# Revit family: HOSPITAIR SCROLAIR 2
name_source: partatom
category: Equipement de génie climatique
revit_build: Autodesk Revit 2018 (Build: 20170223_1515(x64)
units: mm (PartAtom-declared; Revit-internal decimal feet)

## family parameters
Basée sur le plan de construction = Non
Classification = Aucun
Cote de connecteur circulaire = Utiliser le diamètre
Couper avec des vides une fois chargée = Non
Partagée = Non
Point de calcul de pièce = Non
Toujours verticalement = Oui
Type d'élément = Normal

## types (12) — shared parameters
BRANCHEMENT_TERRE = Oui
COS_PHI = 0.9
DIAM_REFOUL_AIR = 20 mm  [stored 0.0656168 ft]
DOUBLE_ALIMENTATION = Oui
LARGEUR = 1135 mm  [stored 3.72375 ft]
NBR_POLES = 1
NEUTRE = Oui
TENSION_ALIM = 400 V
Zone de Maintenance = 600 mm  [stored 1.9685 ft]
Zone de maintenance = Oui
Zone de maintenance_Hauteur = 1565 mm  [stored 5.13451 ft]

## per-type parameters (varying)
| type | AD5035 | AD5065 | DESCR_ALIM_X | DESCR_ALIM_Y | DESCR_REFOUL_AIR | Debit_refoulement_air | HAUTEUR | HAUTEUR_SORTIE AIR | LONGUEUR | LONGUEUR_SORTIE AIR | NIVEAU_SONORE(dB(A)) | POIDS(Kg) | PUISS_APPARENTE | PUISS_ELECT | SCROLAIR G (Version Standard) | Version Capotée |
| HOSPITAIR SCROLAIR 2 - 13SP2 à 10 bar - CAPOTÉE | Oui | Non | Alimentation électrique, 5G1.5mm² | Alimentation électrique, 5G1.5mm² | Refoulement Air; 25.2m3/h; G3/4"FEM | 25.2 m³/h | 1220 mm  [stored 4.00262 ft] | 968 mm | 2340 mm  [stored 7.67717 ft] | 672 mm  [stored 2.20472 ft] | 66 | 570 mm  [stored 1.87008 ft] | 2444 VA | 2 kW | SCROLAIR G - (version standard - Plateau) : 13SP2 - CAPOTÉ | Oui |
| HOSPITAIR SCROLAIR 2 - 29SP2 à 10 bar - CAPOTÉE | Oui | Non | Alimentation électrique, 5G2.5mm² | Alimentation électrique, 5G2.5mm² | Refoulement Air; 58.6m3/h; G3/4"FEM | 58.6 m³/h | 1220 mm  [stored 4.00262 ft] | 968 mm | 2340 mm  [stored 7.67717 ft] | 672 mm  [stored 2.20472 ft] | 67 | 610 mm  [stored 2.00131 ft] | 6111 VA | 6 kW | SCROLAIR G - (version standard - Plateau) : 29SP2 - CAPOTÉ | Oui |
| HOSPITAIR SCROLAIR 2 - 42SP2 à 10 bar - CAPOTÉE | Non | Oui | Alimentation électrique, 5G4mm² | Alimentation électrique, 5G4mm² | Refoulement Air; 84m3/h; G3/4"FEM | 84.0 m³/h | 1570 mm | 1488 mm  [stored 4.88189 ft] | 2485 mm | 699.5 mm | 67 | 635 mm | 8333 VA | 8 kW | SCROLAIR G - (version standard - Plateau) : 42SP2 - CAPOTÉ | Oui |
| HOSPITAIR SCROLAIR 2 - 13SP2 à 10 bar - NON CAPOTÉE | Oui | Non | Alimentation électrique, 5G1.5mm² | Alimentation électrique, 5G1.5mm² | Refoulement Air; 25.2m3/h; G3/4"FEM | 25.2 m³/h | 1180 mm  [stored 3.87139 ft] | 968 mm | 2340 mm  [stored 7.67717 ft] | 672 mm  [stored 2.20472 ft] | 67 | 570 mm  [stored 1.87008 ft] | 2444 VA | 2 kW | SCROLAIR G - (version standard - Plateau) : 13SP2 - STANDARD | Non |
| HOSPITAIR SCROLAIR 2 - 13SP2 à 8 bar - CAPOTÉE | Oui | Non | Alimentation électrique, 5G1.5mm² | Alimentation électrique, 5G1.5mm² | Refoulement Air; 31.2m3/h; G3/4"FEM | 31.2 m³/h | 1220 mm  [stored 4.00262 ft] | 968 mm | 2340 mm  [stored 7.67717 ft] | 672 mm  [stored 2.20472 ft] | 66 | 570 mm  [stored 1.87008 ft] | 2444 VA | 2 kW | SCROLAIR G - (version standard - Plateau) : 13SP2 - CAPOTÉ | Oui |
| HOSPITAIR SCROLAIR 2 - 13SP2 à 8 bar - NON CAPOTÉE | Oui | Non | Alimentation électrique, 5G1.5mm² | Alimentation électrique, 5G1.5mm² | Refoulement Air; 31.2m3/h; G3/4"FEM | 31.2 m³/h | 1180 mm  [stored 3.87139 ft] | 968 mm | 2340 mm  [stored 7.67717 ft] | 672 mm  [stored 2.20472 ft] | 67 | 570 mm  [stored 1.87008 ft] | 2444 VA | 2 kW | SCROLAIR G - (version standard - Plateau) : 13SP2 - STANDARD | Non |
| HOSPITAIR SCROLAIR 2 - 29SP2 à 10 bar - NON CAPOTÉE | Oui | Non | Alimentation électrique, 5G2.5mm² | Alimentation électrique, 5G2.5mm² | Refoulement Air; 58.6m3/h; G3/4"FEM | 58.6 m³/h | 1180 mm  [stored 3.87139 ft] | 968 mm | 2340 mm  [stored 7.67717 ft] | 672 mm  [stored 2.20472 ft] | 68 | 610 mm  [stored 2.00131 ft] | 6111 VA | 6 kW | SCROLAIR G - (version standard - Plateau) : 29SP2 - STANDARD | Non |
| HOSPITAIR SCROLAIR 2 - 29SP2 à 8 bar - CAPOTÉE | Oui | Non | Alimentation électrique, 5G2.5mm² | Alimentation électrique, 5G2.5mm² | Refoulement Air; 72m3/h; G3/4"FEM | 72.0 m³/h | 1220 mm  [stored 4.00262 ft] | 968 mm | 2340 mm  [stored 7.67717 ft] | 672 mm  [stored 2.20472 ft] | 67 | 610 mm  [stored 2.00131 ft] | 6111 VA | 6 kW | SCROLAIR G - (version standard - Plateau) : 29SP2 - CAPOTÉ | Oui |
| HOSPITAIR SCROLAIR 2 - 29SP2 à 8 bar - NON CAPOTÉE | Oui | Non | Alimentation électrique, 5G2.5mm² | Alimentation électrique, 5G2.5mm² | Refoulement Air; 72m3/h; G3/4"FEM | 72.0 m³/h | 1180 mm  [stored 3.87139 ft] | 968 mm | 2340 mm  [stored 7.67717 ft] | 672 mm  [stored 2.20472 ft] | 68 | 610 mm  [stored 2.00131 ft] | 6111 VA | 6 kW | SCROLAIR G - (version standard - Plateau) : 29SP2 - STANDARD | Non |
| HOSPITAIR SCROLAIR 2 - 42SP2 à 10 bar - NON CAPOTÉE | Non | Oui | Alimentation électrique, 5G4mm² | Alimentation électrique, 5G4mm² | Refoulement Air; 84m3/h; G3/4"FEM | 84.0 m³/h | 1570 mm | 1488 mm  [stored 4.88189 ft] | 2485 mm | 699.5 mm | 68 | 635 mm | 8333 VA | 8 kW | SCROLAIR G - (version standard - Plateau) : 42SP2 - STANDARD | Non |
| HOSPITAIR SCROLAIR 2 - 42SP2 à 8 bar - CAPOTÉE | Non | Oui | Alimentation électrique, 5G4mm² | Alimentation électrique, 5G4mm² | Refoulement Air; 104m3/h; G3/4"FEM | 104.0 m³/h | 1570 mm | 1488 mm  [stored 4.88189 ft] | 2485 mm | 699.5 mm | 67 | 635 mm | 8333 VA | 8 kW | SCROLAIR G - (version standard - Plateau) : 42SP2 - CAPOTÉ | Oui |
| HOSPITAIR SCROLAIR 2 - 42SP2 à 8 bar - NON CAPOTÉE | Non | Oui | Alimentation électrique, 5G4mm² | Alimentation électrique, 5G4mm² | Refoulement Air; 104m3/h; G3/4"FEM | 104.0 m³/h | 1570 mm | 1488 mm  [stored 4.88189 ft] | 2485 mm | 699.5 mm | 68 | 635 mm | 8333 VA | 8 kW | SCROLAIR G - (version standard - Plateau) : 42SP2 - STANDARD | Non |

note: [stored X ft] marks values corroborated as IEEE doubles in the binary element streams (Revit-internal decimal feet)

## geometry (parser evidence)
native form markers: Sweep x12
no freeform markers — native parametric forms only
